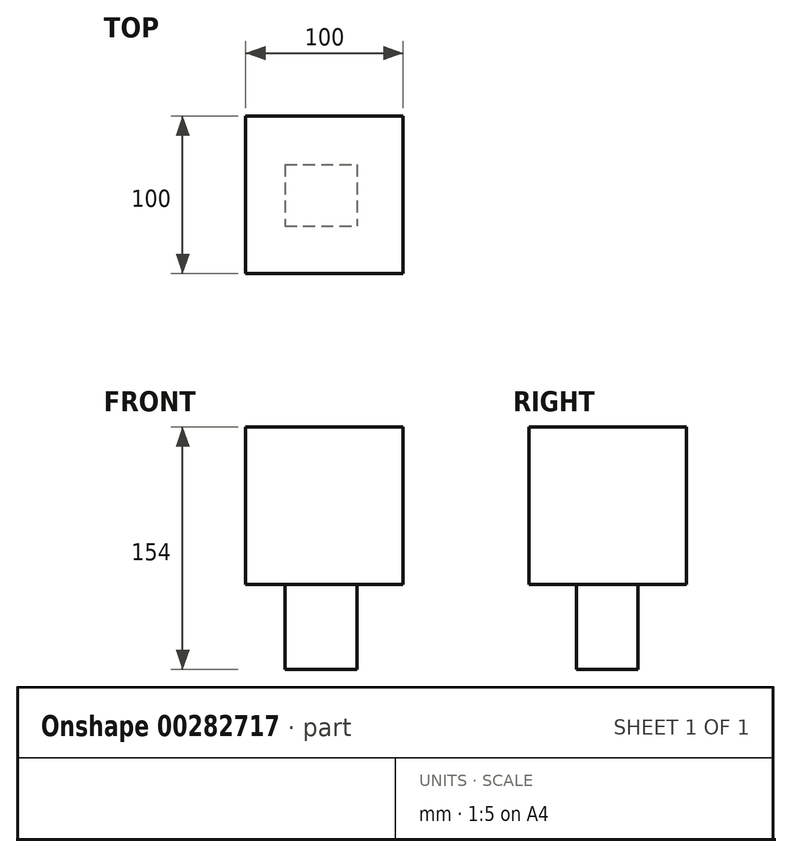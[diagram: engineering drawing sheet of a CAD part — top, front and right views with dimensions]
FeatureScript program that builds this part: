
annotation { "Feature Type Name" : "Feature", "Feature Type Description" : "" }
export const myFeature = defineFeature(function(context is Context, id is Id, definition is map)
    precondition{}
    {
        {
            var Q0;
            Q0=qCreatedBy(makeId("Top.planeOp"),FACE);
            var sketch = newSketch(context, id + "F0", { "sketchPlane" : qUnion([Q0])});
            skLineSegment(sketch, "E0.bottom", {"start": v(0, 0) * mm, "end": v(100, 0) * mm});
            skLineSegment(sketch, "E0.top", {"start": v(0, 100) * mm, "end": v(100, 100) * mm});
            skLineSegment(sketch, "E0.left", {"start": v(0, 0) * mm, "end": v(0, 100) * mm});
            skLineSegment(sketch, "E0.right", {"start": v(100, 0) * mm, "end": v(100, 100) * mm});
            skSolve(sketch);
        }
        {
            var Q0;
            Q0 = qSketchRegion(id + "F0", true);
            var Q1;
            Q1 = qSketchRegion(id + "F2", true);
            extrude(context, id + "F1", {"entities" : qUnion([Q0, Q1]), "depth" : 100 * mm});
        }
        {
            var Q0;
            Q0=makeQuery(id+"F1.opExtrude","CAP_FACE",FACE,{"disambiguationData":[OSD([sQuery(id+"F0.wireOp",EDGE,"E0.bottom"),sQuery(id+"F0.wireOp",EDGE,"E0.top"),sQuery(id+"F0.wireOp",EDGE,"E0.left"),sQuery(id+"F0.wireOp",EDGE,"E0.right")])],"isStart":false});
            var sketch = newSketch(context, id + "F2", { "sketchPlane" : qUnion([Q0])});
            skLineSegment(sketch, "E1.bottom", {"start": v(25.02, 69.23) * mm, "end": v(70.65, 69.23) * mm});
            skLineSegment(sketch, "E1.top", {"start": v(25.02, 30.03) * mm, "end": v(70.65, 30.03) * mm});
            skLineSegment(sketch, "E1.left", {"start": v(25.02, 69.23) * mm, "end": v(25.02, 30.03) * mm});
            skLineSegment(sketch, "E1.right", {"start": v(70.65, 69.23) * mm, "end": v(70.65, 30.03) * mm});
            skSolve(sketch);
        }
        {
            var Q0;
            Q0 = qSketchRegion(id + "F2", true);
            extrude(context, id + "F3", {"entities" : qUnion([Q0]), "operationType" : NewBodyOperationType.ADD, "oppositeDirection" : true, "depth" : 154 * mm});
        }
    });
